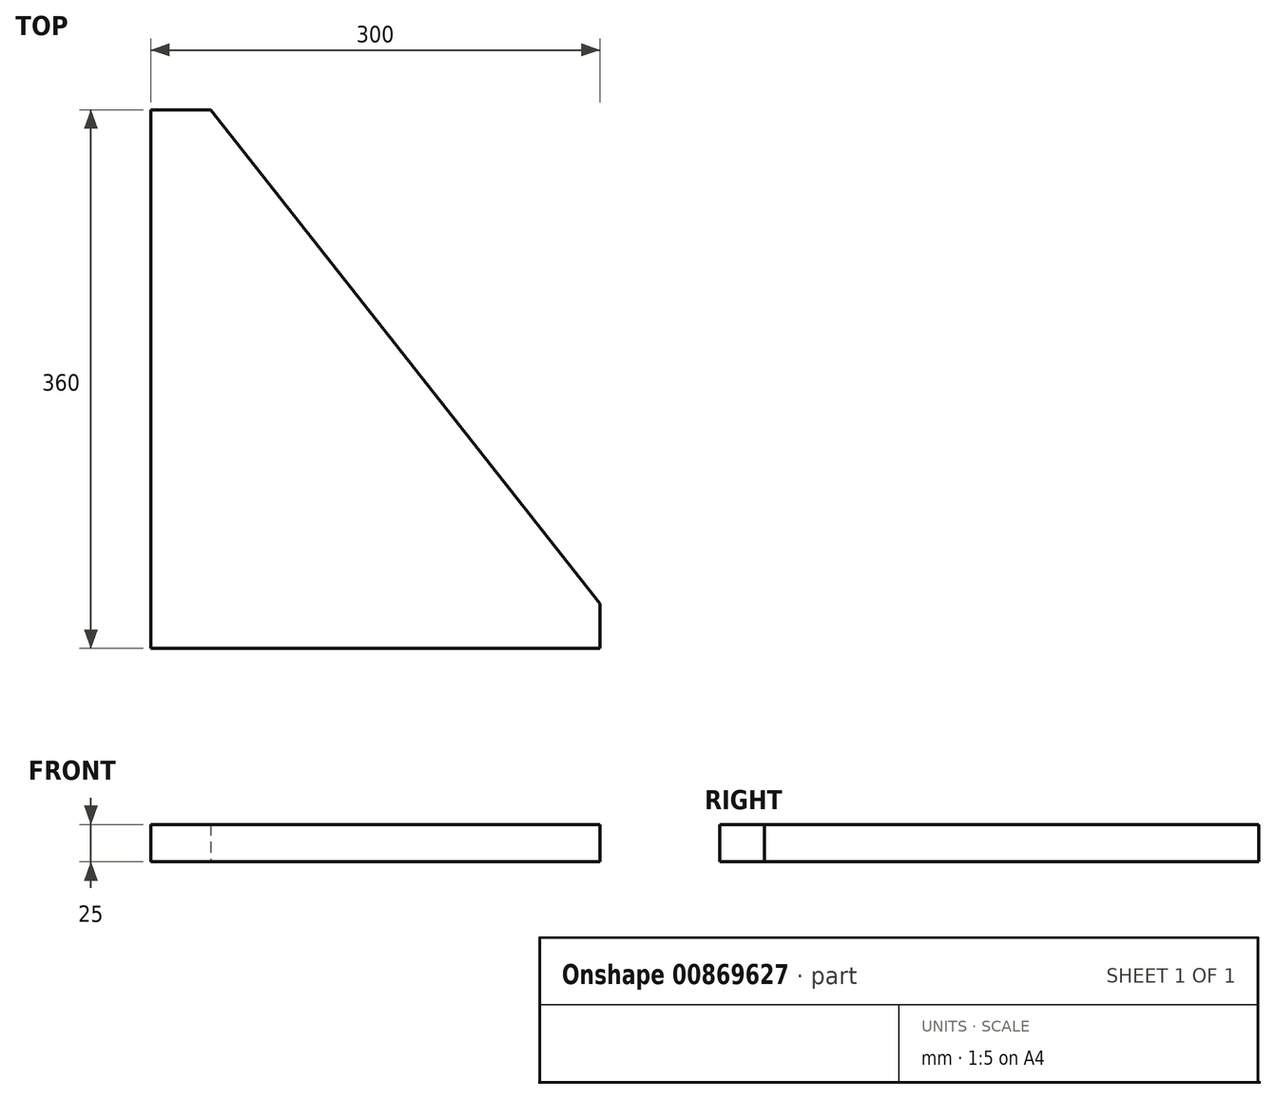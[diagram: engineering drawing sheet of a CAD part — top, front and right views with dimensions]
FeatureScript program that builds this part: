
annotation { "Feature Type Name" : "Feature", "Feature Type Description" : "" }
export const myFeature = defineFeature(function(context is Context, id is Id, definition is map)
    precondition{}
    {
        {
            var Q0;
            Q0=qCreatedBy(makeId("Top.planeOp"),FACE);
            var sketch = newSketch(context, id + "F0", { "sketchPlane" : qUnion([Q0])});
            skLineSegment(sketch, "E0", {"start": v(20, 0) * mm, "end": v(0, 0) * mm});
            skLineSegment(sketch, "E1", {"start": v(0, 0) * mm, "end": v(300, 0) * mm});
            skLineSegment(sketch, "E2", {"start": v(0, 0) * mm, "end": v(0, 330) * mm});
            skLineSegment(sketch, "E3", {"start": v(0, 330) * mm, "end": v(40, 330) * mm});
            skLineSegment(sketch, "E4", {"start": v(40, 330) * mm, "end": v(300, 0) * mm});
            skLineSegment(sketch, "E5", {"start": v(40, 330) * mm, "end": v(40, 297.68) * mm});
            skLineSegment(sketch, "E6", {"start": v(40, 297.68) * mm, "end": v(274.54, 0) * mm});
            skLineSegment(sketch, "E7", {"start": v(274.54, 0) * mm, "end": v(300, 0) * mm});
            skLineSegment(sketch, "E8", {"start": v(40, 297.68) * mm, "end": v(40, 0) * mm});
            skLineSegment(sketch, "E9.top", {"start": v(0, -30) * mm, "end": v(300, -30) * mm});
            skLineSegment(sketch, "E9.left", {"start": v(0, 0) * mm, "end": v(0, -30) * mm});
            skLineSegment(sketch, "E9.right", {"start": v(300, 0) * mm, "end": v(300, -30) * mm});
            skSolve(sketch);
        }
        {
            var Q0;
            {var subQ1=sQuery(id+"F0.wireOp",EDGE,"E0");Q0=makeQuery(id+"F0.imprint","IMPRINT",FACE,{"disambiguationData":[TD([[makeQuery(id+"F0.imprint","IMPRINT",EDGE,{"derivedFrom":subQ1}),-1.0]])]});}
            var Q1;
            {var subQ2=sQuery(id+"F0.wireOp",EDGE,"E6");Q1=makeQuery(id+"F0.imprint","IMPRINT",FACE,{"disambiguationData":[TD([[makeQuery(id+"F0.imprint","IMPRINT",EDGE,{"derivedFrom":subQ2}),-1.0]])]});}
            var Q2;
            {var subQ1=sQuery(id+"F0.wireOp",EDGE,"E0");Q2=makeQuery(id+"F0.imprint","IMPRINT",FACE,{"disambiguationData":[TD([[makeQuery(id+"F0.imprint","IMPRINT",EDGE,{"derivedFrom":subQ1}),1.0]])]});}
            var Q3;
            {var subQ0=sQuery(id+"F0.wireOp",EDGE,"E4");Q3=makeQuery(id+"F0.imprint","IMPRINT",FACE,{"disambiguationData":[TD([[makeQuery(id+"F0.imprint","IMPRINT",EDGE,{"derivedFrom":subQ0}),-1.0]])]});}
            extrude(context, id + "F1", {"entities" : qUnion([Q0, Q1, Q2, Q3]), "depth" : 25 * mm, "offsetDistance" : 25 * mm});
        }
    });
